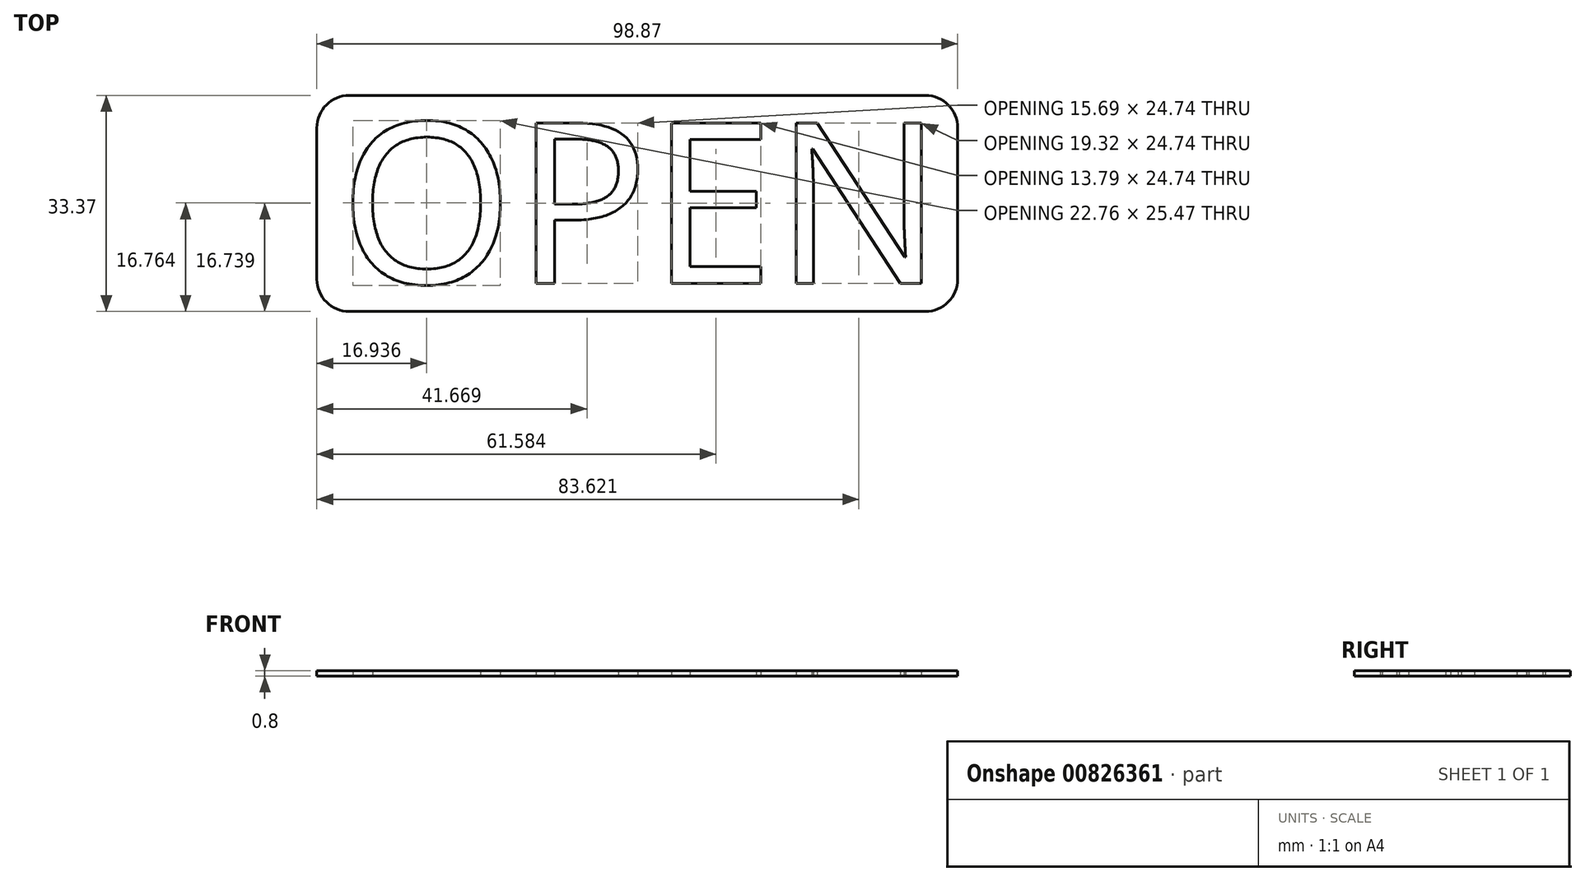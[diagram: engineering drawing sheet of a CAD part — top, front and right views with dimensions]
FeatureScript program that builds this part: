
annotation { "Feature Type Name" : "Feature", "Feature Type Description" : "" }
export const myFeature = defineFeature(function(context is Context, id is Id, definition is map)
    precondition{}
    {
        {
            var Q0;
            Q0=qCreatedBy(makeId("Top.planeOp"),FACE);
            var sketch = newSketch(context, id + "F0", { "sketchPlane" : qUnion([Q0])});
            skText(sketch, "E0", { "text": "OPEN", "fontName": "OpenSans-Regular.ttf"});
            skLineSegment(sketch, "E1.bottom", {"start": v(-44.36, 16.45) * mm, "end": v(44.51, 16.45) * mm});
            skLineSegment(sketch, "E1.top", {"start": v(-44.36, -16.92) * mm, "end": v(44.51, -16.92) * mm});
            skLineSegment(sketch, "E1.left", {"start": v(-49.36, 11.45) * mm, "end": v(-49.36, -11.92) * mm});
            skLineSegment(sketch, "E1.right", {"start": v(49.51, 11.45) * mm, "end": v(49.51, -11.92) * mm});
            skPoint(sketch, "E2.visualSharp", {"position": v(-49.36, 16.45) * mm});
            skArc(sketch, "E2.filletArc", {"start": v(-44.36, 16.45) * mm, "mid": v(-47.9, 14.99) * mm, "end": v(-49.36, 11.45) * mm});
            skPoint(sketch, "E3.visualSharp", {"position": v(-49.36, -16.92) * mm});
            skArc(sketch, "E3.filletArc", {"start": v(-49.36, -11.92) * mm, "mid": v(-47.9, -15.46) * mm, "end": v(-44.36, -16.92) * mm});
            skPoint(sketch, "E4.visualSharp", {"position": v(49.51, -16.92) * mm});
            skArc(sketch, "E4.filletArc", {"start": v(44.51, -16.92) * mm, "mid": v(48.05, -15.46) * mm, "end": v(49.51, -11.92) * mm});
            skPoint(sketch, "E5.visualSharp", {"position": v(49.51, 16.45) * mm});
            skArc(sketch, "E5.filletArc", {"start": v(49.51, 11.45) * mm, "mid": v(48.05, 14.99) * mm, "end": v(44.51, 16.45) * mm});
            const initialGuessF0  = {"E0": [-0.04592, -0.01255, 1, 0, 0.02495]};
            skSetInitialGuess(sketch, initialGuessF0);
            skSolve(sketch);
        }
        {
            var Q0;
            Q0=makeQuery(id+"F0.imprint","IMPRINT",FACE,{"disambiguationData":[TD([[makeQuery(id+"F0.imprint","IMPRINT",EDGE,{"derivedFrom":sQuery(id+"F0.wireOp",EDGE,"E0.sketch_text.stroke-0")}),1.0]])]});
            var Q1;
            Q1=makeQuery(id+"F0.imprint","IMPRINT",FACE,{"disambiguationData":[TD([[makeQuery(id+"F0.imprint","IMPRINT",EDGE,{"derivedFrom":sQuery(id+"F0.wireOp",EDGE,"E0.sketch_text.stroke-8")}),1.0]])]});
            var Q2;
            Q2=makeQuery(id+"F0.imprint","IMPRINT",FACE,{"disambiguationData":[TD([[makeQuery(id+"F0.imprint","IMPRINT",EDGE,{"derivedFrom":sQuery(id+"F0.wireOp",EDGE,"E0.sketch_text.stroke-24")}),1.0]])]});
            extrude(context, id + "F1", {"entities" : qUnion([Q0, Q1, Q2]), "depth" : 0.8 * mm, "offsetDistance" : 25 * mm});
        }
    });
